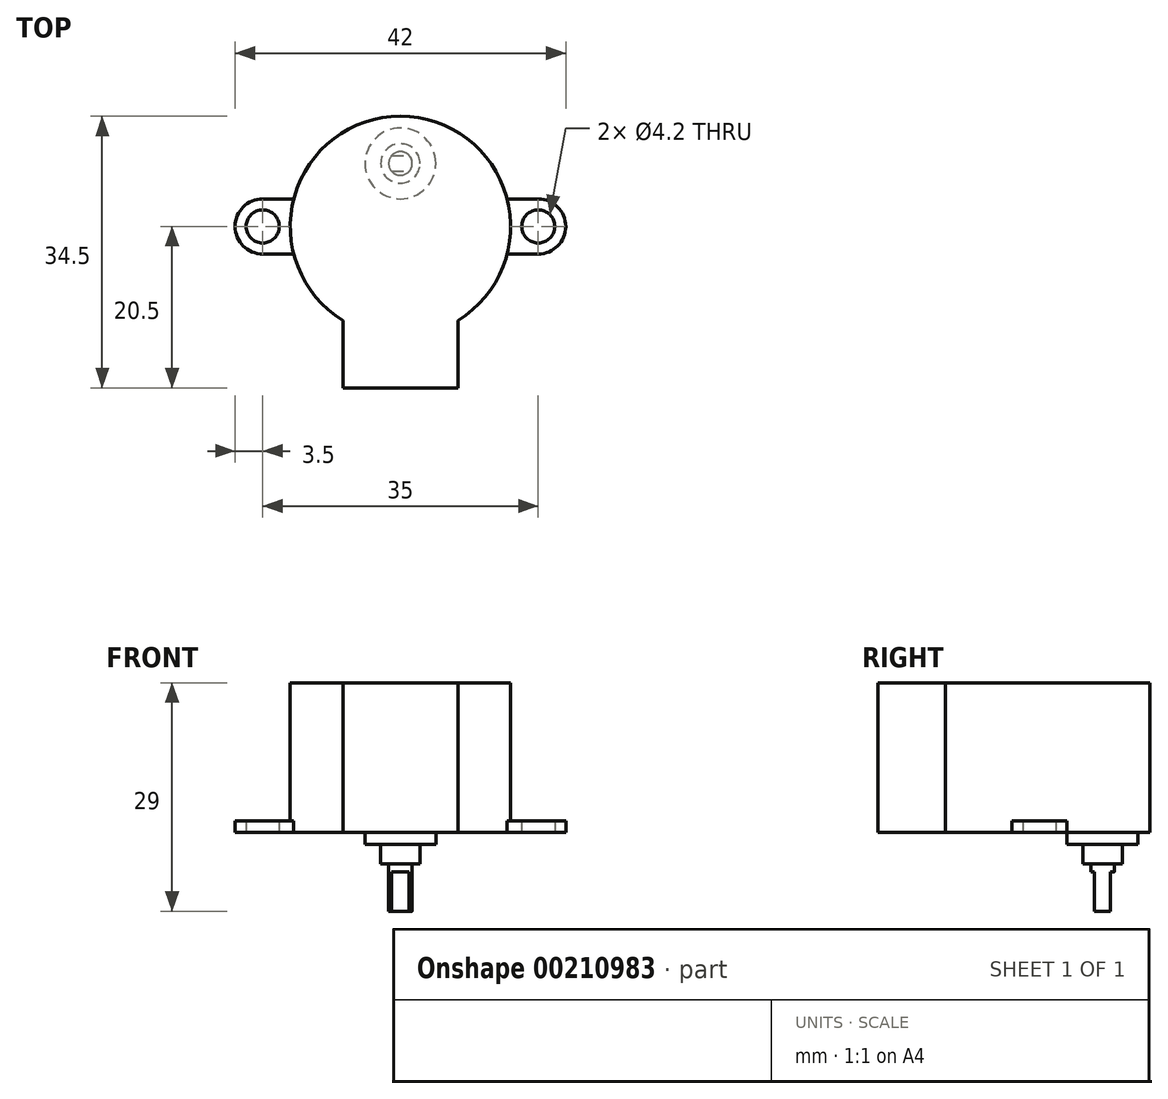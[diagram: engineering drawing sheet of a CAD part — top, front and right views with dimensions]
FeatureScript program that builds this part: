
annotation { "Feature Type Name" : "Feature", "Feature Type Description" : "" }
export const myFeature = defineFeature(function(context is Context, id is Id, definition is map)
    precondition{}
    {
        {
            var Q0;
            Q0=qCreatedBy(makeId("Top.planeOp"),FACE);
            var sketch = newSketch(context, id + "F0", { "sketchPlane" : qUnion([Q0])});
            skCircle(sketch, "E0", {"center": v(0, 0) * mm, "radius": 17.5 * mm, "construction": true});
            skCircle(sketch, "E1", {"center": v(-17.5, 0) * mm, "radius": 2.1 * mm});
            skCircle(sketch, "E2", {"center": v(17.5, 0) * mm, "radius": 2.1 * mm});
            skArc(sketch, "E3", {"start": v(-17.15, 3.48) * mm, "mid": v(-21, 0) * mm, "end": v(-17.15, -3.48) * mm});
            skArc(sketch, "E4", {"start": v(17.15, -3.48) * mm, "mid": v(21, 0) * mm, "end": v(17.15, 3.48) * mm});
            skCircle(sketch, "E5", {"center": v(0, 8) * mm, "radius": 1.5 * mm});
            skLineSegment(sketch, "E6", {"start": v(-7.3, -20.5) * mm, "end": v(7.3, -20.5) * mm});
            skLineSegment(sketch, "E7", {"start": v(0, 0) * mm, "end": v(0, -20.5) * mm, "construction": true});
            skLineSegment(sketch, "E8", {"start": v(-17.5, -3.5) * mm, "end": v(-13.56, -3.5) * mm});
            skLineSegment(sketch, "E9", {"start": v(-17.5, 3.5) * mm, "end": v(-13.56, 3.5) * mm});
            skArc(sketch, "E10", {"start": v(7.3, -11.95) * mm, "mid": v(0, 14) * mm, "end": v(-7.3, -11.95) * mm});
            skCircle(sketch, "E11", {"center": v(0, 8) * mm, "radius": 4.5 * mm});
            skCircle(sketch, "E12", {"center": v(0, 8) * mm, "radius": 2.5 * mm});
            skLineSegment(sketch, "E13", {"start": v(-1.12, 9) * mm, "end": v(1.12, 9) * mm});
            skLineSegment(sketch, "E14", {"start": v(-1.12, 7) * mm, "end": v(1.12, 7) * mm});
            skLineSegment(sketch, "E15", {"start": v(-7.3, -20.5) * mm, "end": v(-7.3, -11.95) * mm});
            skLineSegment(sketch, "E16", {"start": v(7.3, -20.5) * mm, "end": v(7.3, -11.95) * mm});
            skLineSegment(sketch, "E17.trimOffspring", {"start": v(13.56, 3.5) * mm, "end": v(17.5, 3.5) * mm});
            skLineSegment(sketch, "E18.trimOffspring", {"start": v(13.56, -3.5) * mm, "end": v(17.5, -3.5) * mm});
            skSolve(sketch);
        }
        {
            var Q0;
            Q0=makeQuery(id+"F0.imprint","IMPRINT",FACE,{"disambiguationData":[TD([[makeQuery(id+"F0.imprint","IMPRINT",EDGE,{"derivedFrom":sQuery(id+"F0.wireOp",EDGE,"E6")}),1.0]])]});
            extrude(context, id + "F1", {"entities" : qUnion([Q0]), "depth" : 19 * mm});
        }
        {
            var Q0;
            Q0=makeQuery(id+"F0.imprint","IMPRINT",FACE,{"disambiguationData":[TD([[makeQuery(id+"F0.imprint","IMPRINT",EDGE,{"derivedFrom":sQuery(id+"F0.wireOp",EDGE,"E1")}),-1.0]])]});
            var Q1;
            Q1=makeQuery(id+"F0.imprint","IMPRINT",FACE,{"disambiguationData":[TD([[makeQuery(id+"F0.imprint","IMPRINT",EDGE,{"derivedFrom":sQuery(id+"F0.wireOp",EDGE,"E2")}),-1.0]])]});
            extrude(context, id + "F2", {"entities" : qUnion([Q0, Q1]), "operationType" : NewBodyOperationType.ADD, "depth" : 1.5 * mm});
        }
        {
            var Q0;
            Q0=makeQuery(id+"F0.imprint","IMPRINT",FACE,{"disambiguationData":[TD([[makeQuery(id+"F0.imprint","IMPRINT",EDGE,{"derivedFrom":sQuery(id+"F0.wireOp",EDGE,"E11")}),1.0]])]});
            extrude(context, id + "F3", {"entities" : qUnion([Q0]), "operationType" : NewBodyOperationType.ADD, "oppositeDirection" : true, "depth" : 1.5 * mm, "hasSecondDirection" : true, "secondDirectionOppositeDirection" : false, "secondDirectionDepth" : 19 * mm});
        }
        {
            var Q0;
            Q0=makeQuery(id+"F0.imprint","IMPRINT",FACE,{"disambiguationData":[TD([[makeQuery(id+"F0.imprint","IMPRINT",EDGE,{"derivedFrom":sQuery(id+"F0.wireOp",EDGE,"E12")}),1.0]])]});
            extrude(context, id + "F4", {"entities" : qUnion([Q0]), "operationType" : NewBodyOperationType.ADD, "oppositeDirection" : true, "depth" : 4 * mm, "hasSecondDirection" : true, "secondDirectionOppositeDirection" : false, "secondDirectionDepth" : 19 * mm});
        }
        {
            var Q0;
            {var subQ0=sQuery(id+"F0.wireOp",EDGE,"E13");Q0=makeQuery(id+"F0.imprint","IMPRINT",FACE,{"disambiguationData":[TD([[makeQuery(id+"F0.imprint","IMPRINT",EDGE,{"derivedFrom":subQ0}),-1.0]])]});}
            extrude(context, id + "F5", {"entities" : qUnion([Q0]), "operationType" : NewBodyOperationType.ADD, "oppositeDirection" : true, "depth" : 10 * mm, "hasSecondDirection" : true, "secondDirectionOppositeDirection" : false, "secondDirectionDepth" : 19 * mm});
        }
        {
            var Q0;
            {var subQ0=sQuery(id+"F0.wireOp",EDGE,"E14");Q0=makeQuery(id+"F0.imprint","IMPRINT",FACE,{"disambiguationData":[TD([[makeQuery(id+"F0.imprint","IMPRINT",EDGE,{"derivedFrom":subQ0}),-1.0]])]});}
            var Q1;
            {var subQ0=sQuery(id+"F0.wireOp",EDGE,"E13");Q1=makeQuery(id+"F0.imprint","IMPRINT",FACE,{"disambiguationData":[TD([[makeQuery(id+"F0.imprint","IMPRINT",EDGE,{"derivedFrom":subQ0}),1.0]])]});}
            extrude(context, id + "F6", {"entities" : qUnion([Q0, Q1]), "operationType" : NewBodyOperationType.ADD, "depth" : 19 * mm, "hasSecondDirection" : true, "secondDirectionOppositeDirection" : true, "secondDirectionDepth" : 5 * mm});
        }
    });
